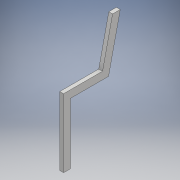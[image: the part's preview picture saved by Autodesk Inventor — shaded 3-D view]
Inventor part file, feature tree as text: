
AUTODESK INVENTOR PART (.ipt)
format: ipt  version: 2017 (Build 210142000, 142)  size: 103,936 bytes
history: native  units: mm
features: extrude x1, sketch x1
ambient origin geometry x8: Origin, YZ Plane, XZ Plane, XY Plane, X Axis, Y Axis, Z Axis, Center Point
bodies: Solide1 (feature_tree)
feature tree (2):
  extrude  "Extrusion1"  Depth=45.0mm
  sketch  "Esquisse1"
